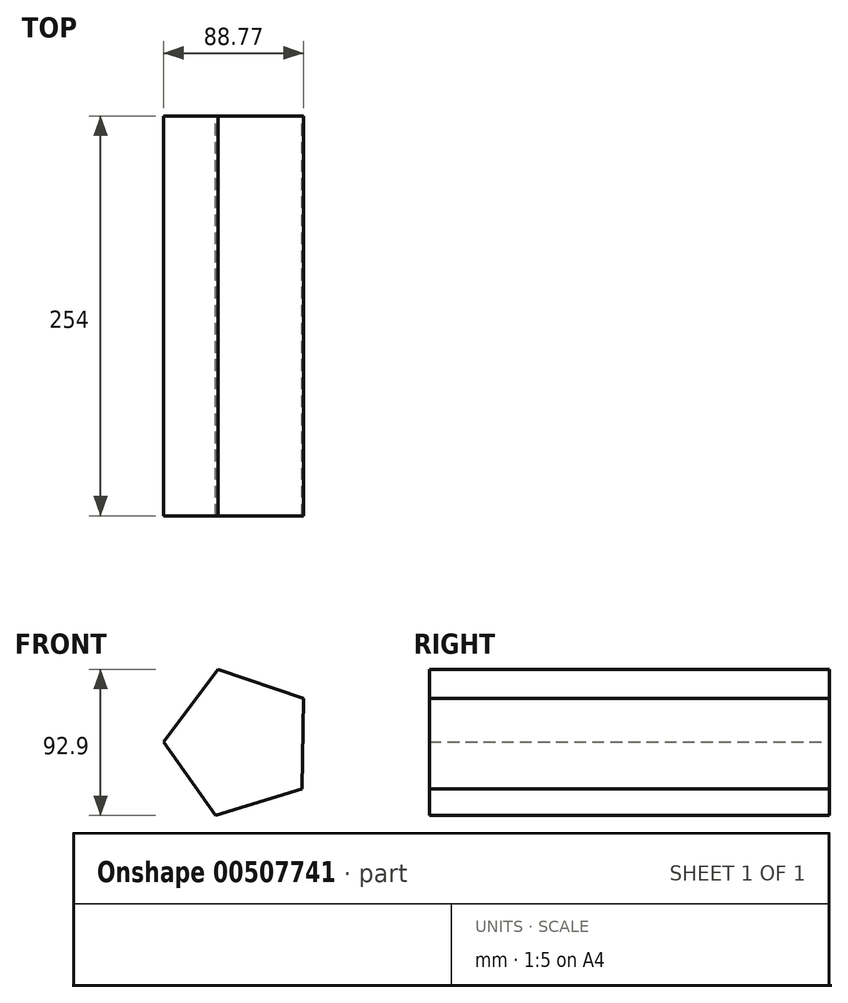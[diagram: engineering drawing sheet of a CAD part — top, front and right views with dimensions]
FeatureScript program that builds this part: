
annotation { "Feature Type Name" : "Feature", "Feature Type Description" : "" }
export const myFeature = defineFeature(function(context is Context, id is Id, definition is map)
    precondition{}
    {
        {
            var Q0;
            Q0=qCreatedBy(makeId("Front.planeOp"),FACE);
            var sketch = newSketch(context, id + "F0", { "sketchPlane" : qUnion([Q0])});
            skCircle(sketch, "E0.cCircle", {"center": v(0, 0) * mm, "radius": 48.84 * mm, "construction": true});
            skLineSegment(sketch, "E0.0", {"start": v(39.93, 28.13) * mm, "end": v(39.1, -29.29) * mm});
            skLineSegment(sketch, "E0.1", {"start": v(39.1, -29.29) * mm, "end": v(-15.77, -46.23) * mm});
            skLineSegment(sketch, "E0.2", {"start": v(-15.77, -46.23) * mm, "end": v(-48.84, 0.72) * mm});
            skLineSegment(sketch, "E0.3", {"start": v(-48.84, 0.72) * mm, "end": v(-14.41, 46.67) * mm});
            skLineSegment(sketch, "E0.4", {"start": v(-14.41, 46.67) * mm, "end": v(39.93, 28.13) * mm});
            skSolve(sketch);
        }
        {
            var Q0;
            Q0=makeQuery(id+"F0.imprint","IMPRINT",FACE,{"disambiguationData":[TD([[makeQuery(id+"F0.imprint","IMPRINT",EDGE,{"derivedFrom":sQuery(id+"F0.wireOp",EDGE,"E0.0")}),-1.0]])]});
            extrude(context, id + "F1", {"entities" : qUnion([Q0]), "depth" : 254 * mm});
        }
    });
